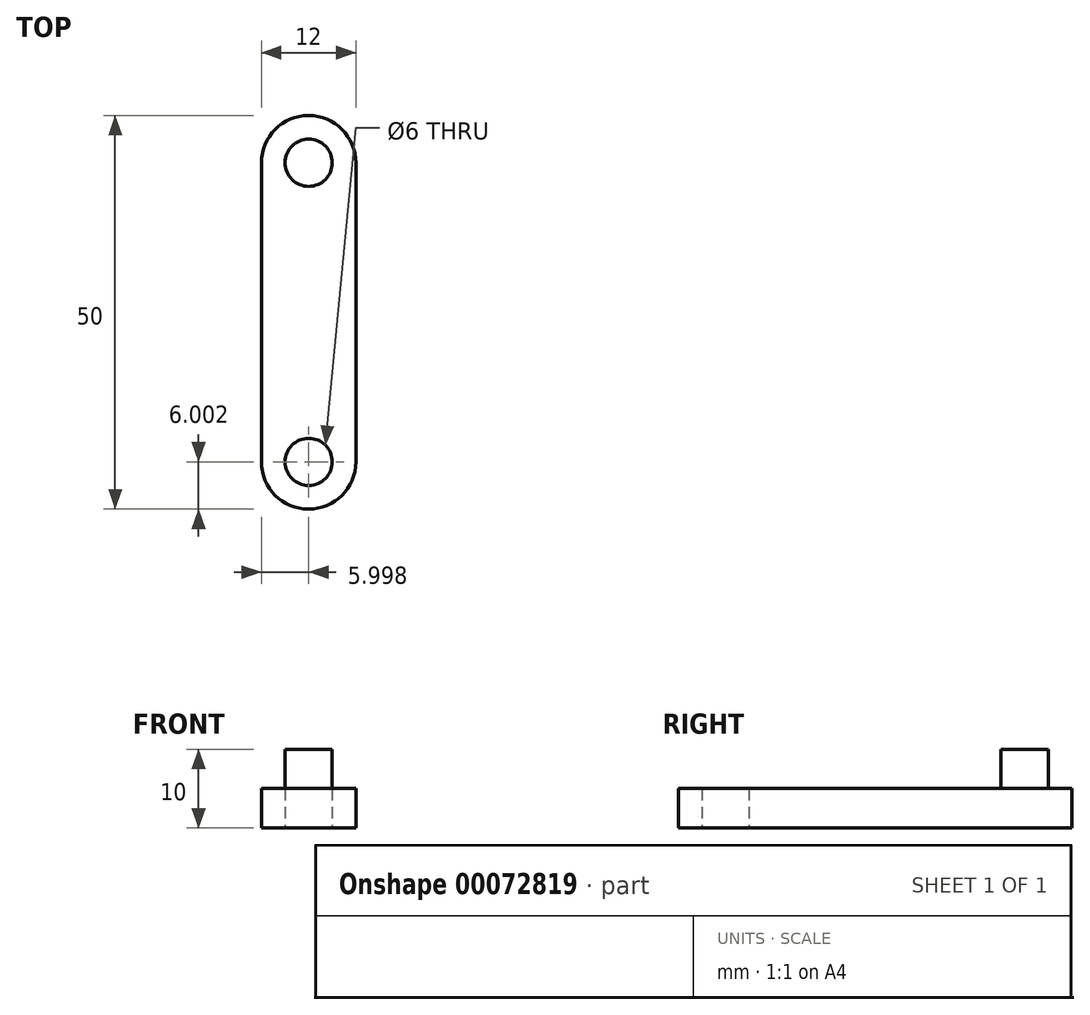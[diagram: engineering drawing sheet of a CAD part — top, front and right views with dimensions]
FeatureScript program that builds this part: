
annotation { "Feature Type Name" : "Feature", "Feature Type Description" : "" }
export const myFeature = defineFeature(function(context is Context, id is Id, definition is map)
    precondition{}
    {
        {
            var Q0;
            Q0=qCreatedBy(makeId("Top.planeOp"),FACE);
            var sketch = newSketch(context, id + "F0", { "sketchPlane" : qUnion([Q0])});
            skLineSegment(sketch, "E0.rect.bottom", {"start": v(5.13, 16.42) * mm, "end": v(-6.87, 16.42) * mm});
            skLineSegment(sketch, "E0.rect.top", {"start": v(5.13, -33.58) * mm, "end": v(-6.87, -33.58) * mm});
            skLineSegment(sketch, "E0.rect.left", {"start": v(5.13, 16.42) * mm, "end": v(5.13, -33.58) * mm});
            skLineSegment(sketch, "E0.rect.right", {"start": v(-6.87, 16.42) * mm, "end": v(-6.87, -33.58) * mm});
            skPoint(sketch, "E0.rect.middle", {"position": v(-0.87, -8.58) * mm});
            skCircle(sketch, "E1", {"center": v(-0.87, -27.58) * mm, "radius": 3 * mm});
            skCircle(sketch, "E2", {"center": v(-0.87, 10.42) * mm, "radius": 3 * mm});
            skSolve(sketch);
        }
        {
            var Q0;
            Q0=makeQuery(id+"F0.imprint","IMPRINT",FACE,{"disambiguationData":[TD([[makeQuery(id+"F0.imprint","IMPRINT",EDGE,{"derivedFrom":sQuery(id+"F0.wireOp",EDGE,"E0.rect.bottom")}),1.0]])]});
            extrude(context, id + "F1", {"entities" : qUnion([Q0]), "depth" : 5 * mm});
        }
        {
            var Q0;
            Q0=makeQuery(id+"F1.opExtrude","SWEPT_EDGE",EDGE,{"disambiguationData":[OSD([sQuery(id+"F0.wireOp",EDGE,"E0.rect.bottom"),sQuery(id+"F0.wireOp",EDGE,"E0.rect.right")])]});
            var Q1;
            Q1=makeQuery(id+"F1.opExtrude","SWEPT_EDGE",EDGE,{"disambiguationData":[OSD([sQuery(id+"F0.wireOp",EDGE,"E0.rect.bottom"),sQuery(id+"F0.wireOp",EDGE,"E0.rect.left")])]});
            var Q2;
            Q2=makeQuery(id+"F1.opExtrude","SWEPT_EDGE",EDGE,{"disambiguationData":[OSD([sQuery(id+"F0.wireOp",EDGE,"E0.rect.top"),sQuery(id+"F0.wireOp",EDGE,"E0.rect.left")])]});
            var Q3;
            Q3=makeQuery(id+"F1.opExtrude","SWEPT_EDGE",EDGE,{"disambiguationData":[OSD([sQuery(id+"F0.wireOp",EDGE,"E0.rect.top"),sQuery(id+"F0.wireOp",EDGE,"E0.rect.right")])]});
            fillet(context, id + "F2", {"entities" : qUnion([Q0, Q1, Q2, Q3]), "radius" : 6 * mm, "tangentPropagation" : true, "allowEdgeOverflow" : false});
        }
        {
            var Q0;
            Q0=makeQuery(id+"F0.imprint","IMPRINT",FACE,{"disambiguationData":[TD([[makeQuery(id+"F0.imprint","IMPRINT",EDGE,{"derivedFrom":sQuery(id+"F0.wireOp",EDGE,"E2")}),1.0]])]});
            extrude(context, id + "F3", {"entities" : qUnion([Q0]), "operationType" : NewBodyOperationType.ADD, "depth" : 10 * mm});
        }
    });
